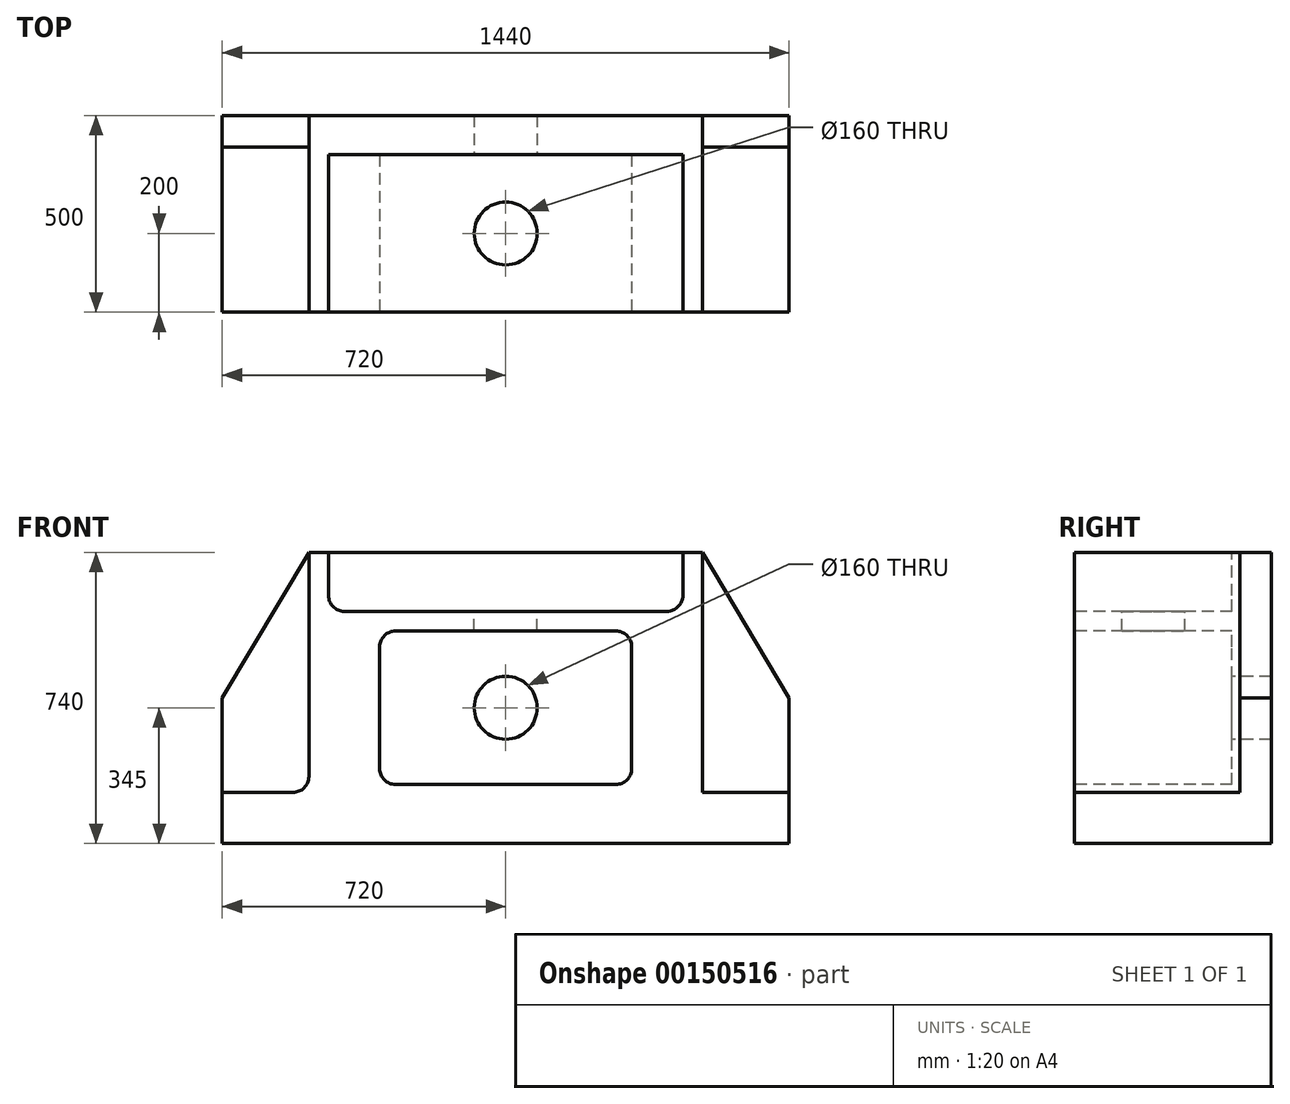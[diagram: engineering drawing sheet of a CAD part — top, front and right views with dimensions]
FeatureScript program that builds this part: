
annotation { "Feature Type Name" : "Feature", "Feature Type Description" : "" }
export const myFeature = defineFeature(function(context is Context, id is Id, definition is map)
    precondition{}
    {
        {
            var Q0;
            Q0=qCreatedBy(makeId("Top.planeOp"),FACE);
            var sketch = newSketch(context, id + "F0", { "sketchPlane" : qUnion([Q0])});
            skLineSegment(sketch, "E0.bottom", {"start": v(720, -250) * mm, "end": v(-720, -250) * mm});
            skLineSegment(sketch, "E0.top", {"start": v(720, 250) * mm, "end": v(-720, 250) * mm});
            skLineSegment(sketch, "E0.left", {"start": v(720, -250) * mm, "end": v(720, 250) * mm});
            skLineSegment(sketch, "E0.right", {"start": v(-720, -250) * mm, "end": v(-720, 250) * mm});
            skPoint(sketch, "E0.middle", {"position": v(0, 0) * mm});
            skSolve(sketch);
        }
        {
            var Q0;
            Q0 = qSketchRegion(id + "F0", true);
            extrude(context, id + "F1", {"entities" : qUnion([Q0]), "depth" : 130 * mm});
        }
        {
            var Q0;
            Q0=makeQuery(id+"F1.opExtrude","CAP_FACE",FACE,{"disambiguationData":[OSD([sQuery(id+"F0.wireOp",EDGE,"E0.bottom"),sQuery(id+"F0.wireOp",EDGE,"E0.top"),sQuery(id+"F0.wireOp",EDGE,"E0.left"),sQuery(id+"F0.wireOp",EDGE,"E0.right")])],"isStart":false});
            var sketch = newSketch(context, id + "F2", { "sketchPlane" : qUnion([Q0])});
            skLineSegment(sketch, "E1.bottom", {"start": v(500, -250) * mm, "end": v(-500, -250) * mm});
            skLineSegment(sketch, "E1.top", {"start": v(500, 250) * mm, "end": v(-500, 250) * mm});
            skLineSegment(sketch, "E1.left", {"start": v(500, -250) * mm, "end": v(500, 250) * mm});
            skLineSegment(sketch, "E1.right", {"start": v(-500, -250) * mm, "end": v(-500, 250) * mm});
            skPoint(sketch, "E1.middle", {"position": v(0, 0) * mm});
            skSolve(sketch);
        }
        {
            var Q0;
            Q0 = qSketchRegion(id + "F2", true);
            extrude(context, id + "F3", {"entities" : qUnion([Q0]), "operationType" : NewBodyOperationType.ADD, "depth" : 610 * mm});
        }
        {
            var Q0;
            Q0=makeQuery(id+"F3.boolean.opBoolean","MERGE",FACE,{"derivedFrom":[makeQuery(id+"F1.opExtrude","SWEPT_FACE",FACE,{"disambiguationData":[OSD([sQuery(id+"F0.wireOp",EDGE,"E0.bottom")])]}),makeQuery(id+"F3.opExtrude","SWEPT_FACE",FACE,{"disambiguationData":[OSD([sQuery(id+"F2.wireOp",EDGE,"E1.bottom")])]})]});
            var sketch = newSketch(context, id + "F4", { "sketchPlane" : qUnion([Q0])});
            skLineSegment(sketch, "E2.bottom", {"start": v(320, 150) * mm, "end": v(-320, 150) * mm});
            skLineSegment(sketch, "E2.top", {"start": v(320, 540) * mm, "end": v(-320, 540) * mm});
            skLineSegment(sketch, "E2.left", {"start": v(320, 150) * mm, "end": v(320, 540) * mm});
            skLineSegment(sketch, "E2.right", {"start": v(-320, 150) * mm, "end": v(-320, 540) * mm});
            skPoint(sketch, "E2.middle", {"position": v(0, 345) * mm});
            skSolve(sketch);
        }
        {
            var Q0;
            Q0 = qSketchRegion(id + "F4", true);
            extrude(context, id + "F5", {"entities" : qUnion([Q0]), "operationType" : NewBodyOperationType.REMOVE, "oppositeDirection" : true, "depth" : 400 * mm});
        }
        {
            var Q0;
            Q0=makeQuery(id+"F5.boolean.opBoolean","COPY",FACE,{"derivedFrom":makeQuery(id+"F5.opExtrude","CAP_FACE",FACE,{"disambiguationData":[OSD([sQuery(id+"F4.wireOp",EDGE,"E2.bottom"),sQuery(id+"F4.wireOp",EDGE,"E2.top"),sQuery(id+"F4.wireOp",EDGE,"E2.left"),sQuery(id+"F4.wireOp",EDGE,"E2.right")])],"isStart":false})});
            var sketch = newSketch(context, id + "F6", { "sketchPlane" : qUnion([Q0])});
            skCircle(sketch, "E3", {"center": v(0, 345) * mm, "radius": 80 * mm});
            skSolve(sketch);
        }
        {
            var Q0;
            Q0=makeQuery(id+"F6.imprint","IMPRINT",FACE,{"disambiguationData":[TD([[makeQuery(id+"F6.imprint","IMPRINT",EDGE,{"derivedFrom":sQuery(id+"F6.wireOp",EDGE,"E3")}),1.0]])]});
            extrude(context, id + "F7", {"entities" : qUnion([Q0]), "operationType" : NewBodyOperationType.REMOVE, "endBound" : BoundingType.THROUGH_ALL, "oppositeDirection" : true, "depth" : 25 * mm});
        }
        {
            var Q0;
            Q0=makeQuery(id+"F3.opExtrude","CAP_FACE",FACE,{"disambiguationData":[OSD([sQuery(id+"F2.wireOp",EDGE,"E1.bottom"),sQuery(id+"F2.wireOp",EDGE,"E1.top"),sQuery(id+"F2.wireOp",EDGE,"E1.left"),sQuery(id+"F2.wireOp",EDGE,"E1.right")])],"isStart":false});
            var sketch = newSketch(context, id + "F8", { "sketchPlane" : qUnion([Q0])});
            skLineSegment(sketch, "E4.bottom", {"start": v(450, 150) * mm, "end": v(-450, 150) * mm});
            skLineSegment(sketch, "E4.top", {"start": v(450, -650) * mm, "end": v(-450, -650) * mm});
            skLineSegment(sketch, "E4.left", {"start": v(450, 150) * mm, "end": v(450, -650) * mm});
            skLineSegment(sketch, "E4.right", {"start": v(-450, 150) * mm, "end": v(-450, -650) * mm});
            skPoint(sketch, "E4.middle", {"position": v(0, -250) * mm});
            skSolve(sketch);
        }
        {
            var Q0;
            Q0 = qSketchRegion(id + "F8", true);
            extrude(context, id + "F9", {"entities" : qUnion([Q0]), "operationType" : NewBodyOperationType.REMOVE, "oppositeDirection" : true, "depth" : 150 * mm});
        }
        {
            var Q0;
            Q0=makeQuery(id+"F9.boolean.opBoolean","COPY",FACE,{"derivedFrom":makeQuery(id+"F9.opExtrude","CAP_FACE",FACE,{"disambiguationData":[OSD([sQuery(id+"F8.wireOp",EDGE,"E4.bottom"),sQuery(id+"F8.wireOp",EDGE,"E4.top"),sQuery(id+"F8.wireOp",EDGE,"E4.left"),sQuery(id+"F8.wireOp",EDGE,"E4.right")])],"isStart":false})});
            var sketch = newSketch(context, id + "F10", { "sketchPlane" : qUnion([Q0])});
            skCircle(sketch, "E5", {"center": v(0, -50) * mm, "radius": 80 * mm});
            skSolve(sketch);
        }
        {
            var Q0;
            Q0=makeQuery(id+"F10.imprint","IMPRINT",FACE,{"disambiguationData":[TD([[makeQuery(id+"F10.imprint","IMPRINT",EDGE,{"derivedFrom":sQuery(id+"F10.wireOp",EDGE,"E5")}),1.0]])]});
            extrude(context, id + "F11", {"entities" : qUnion([Q0]), "operationType" : NewBodyOperationType.REMOVE, "endBound" : BoundingType.UP_TO_NEXT, "oppositeDirection" : true, "depth" : 25 * mm});
        }
        {
            var Q0;
            Q0=makeQuery(id+"F9.boolean.opBoolean","COPY",EDGE,{"derivedFrom":makeQuery(id+"F9.opExtrude","CAP_EDGE",EDGE,{"disambiguationData":[OSD([sQuery(id+"F8.wireOp",EDGE,"E4.left")])],"isStart":false})});
            var Q1;
            Q1=makeQuery(id+"F9.boolean.opBoolean","COPY",EDGE,{"derivedFrom":makeQuery(id+"F9.opExtrude","CAP_EDGE",EDGE,{"disambiguationData":[OSD([sQuery(id+"F8.wireOp",EDGE,"E4.right")])],"isStart":false})});
            var Q2;
            Q2=makeQuery(id+"F3.opExtrude","CAP_EDGE",EDGE,{"disambiguationData":[OSD([sQuery(id+"F2.wireOp",EDGE,"E1.left")])],"isStart":true});
            var Q3;
            Q3=makeQuery(id+"F3.opExtrude","CAP_EDGE",EDGE,{"disambiguationData":[OSD([sQuery(id+"F2.wireOp",EDGE,"E1.right")])],"isStart":true});
            var Q4;
            Q4=makeQuery(id+"F5.boolean.opBoolean","COPY",EDGE,{"derivedFrom":makeQuery(id+"F5.opExtrude","SWEPT_EDGE",EDGE,{"disambiguationData":[OSD([sQuery(id+"F4.wireOp",EDGE,"E2.top"),sQuery(id+"F4.wireOp",EDGE,"E2.right")])]})});
            var Q5;
            Q5=makeQuery(id+"F5.boolean.opBoolean","COPY",EDGE,{"derivedFrom":makeQuery(id+"F5.opExtrude","SWEPT_EDGE",EDGE,{"disambiguationData":[OSD([sQuery(id+"F4.wireOp",EDGE,"E2.bottom"),sQuery(id+"F4.wireOp",EDGE,"E2.right")])]})});
            var Q6;
            Q6=makeQuery(id+"F5.boolean.opBoolean","COPY",EDGE,{"derivedFrom":makeQuery(id+"F5.opExtrude","SWEPT_EDGE",EDGE,{"disambiguationData":[OSD([sQuery(id+"F4.wireOp",EDGE,"E2.top"),sQuery(id+"F4.wireOp",EDGE,"E2.left")])]})});
            var Q7;
            Q7=makeQuery(id+"F5.boolean.opBoolean","COPY",EDGE,{"derivedFrom":makeQuery(id+"F5.opExtrude","SWEPT_EDGE",EDGE,{"disambiguationData":[OSD([sQuery(id+"F4.wireOp",EDGE,"E2.bottom"),sQuery(id+"F4.wireOp",EDGE,"E2.left")])]})});
            fillet(context, id + "F12", {"entities" : qUnion([Q0, Q1, Q2, Q3, Q4, Q5, Q6, Q7]), "radius" : 40 * mm, "tangentPropagation" : true, "allowEdgeOverflow" : false});
        }
        {
            var Q0;
            Q0=makeQuery(id+"F3.boolean.opBoolean","MERGE",FACE,{"derivedFrom":[makeQuery(id+"F1.opExtrude","SWEPT_FACE",FACE,{"disambiguationData":[OSD([sQuery(id+"F0.wireOp",EDGE,"E0.top")])]}),makeQuery(id+"F3.opExtrude","SWEPT_FACE",FACE,{"disambiguationData":[OSD([sQuery(id+"F2.wireOp",EDGE,"E1.top")])]})]});
            var sketch = newSketch(context, id + "F13", { "sketchPlane" : qUnion([Q0])});
            skLineSegment(sketch, "E6", {"start": v(-720, 130) * mm, "end": v(-720, 370) * mm});
            skLineSegment(sketch, "E7", {"start": v(-720, 370) * mm, "end": v(-500, 740) * mm});
            skLineSegment(sketch, "E8", {"start": v(720, 130) * mm, "end": v(720, 370) * mm});
            skLineSegment(sketch, "E9", {"start": v(720, 370) * mm, "end": v(500, 740) * mm});
            skSolve(sketch);
        }
        {
            var Q0;
            Q0 = qSketchRegion(id + "F13", true);
            var Q1;
            Q1=makeQuery(id+"F13.imprint","IMPRINT",FACE,{"disambiguationData":[TD([[makeQuery(id+"F13.imprint","IMPRINT",EDGE,{"derivedFrom":sQuery(id+"F13.wireOp",EDGE,"E8")}),1.0]])]});
            var Q2;
            Q2=makeQuery(id+"F13.imprint","IMPRINT",FACE,{"disambiguationData":[TD([[makeQuery(id+"F13.imprint","IMPRINT",EDGE,{"derivedFrom":sQuery(id+"F13.wireOp",EDGE,"E6")}),-1.0]])]});
            extrude(context, id + "F14", {"entities" : qUnion([Q0, Q1, Q2]), "operationType" : NewBodyOperationType.ADD, "oppositeDirection" : true, "depth" : 80 * mm});
        }
    });
